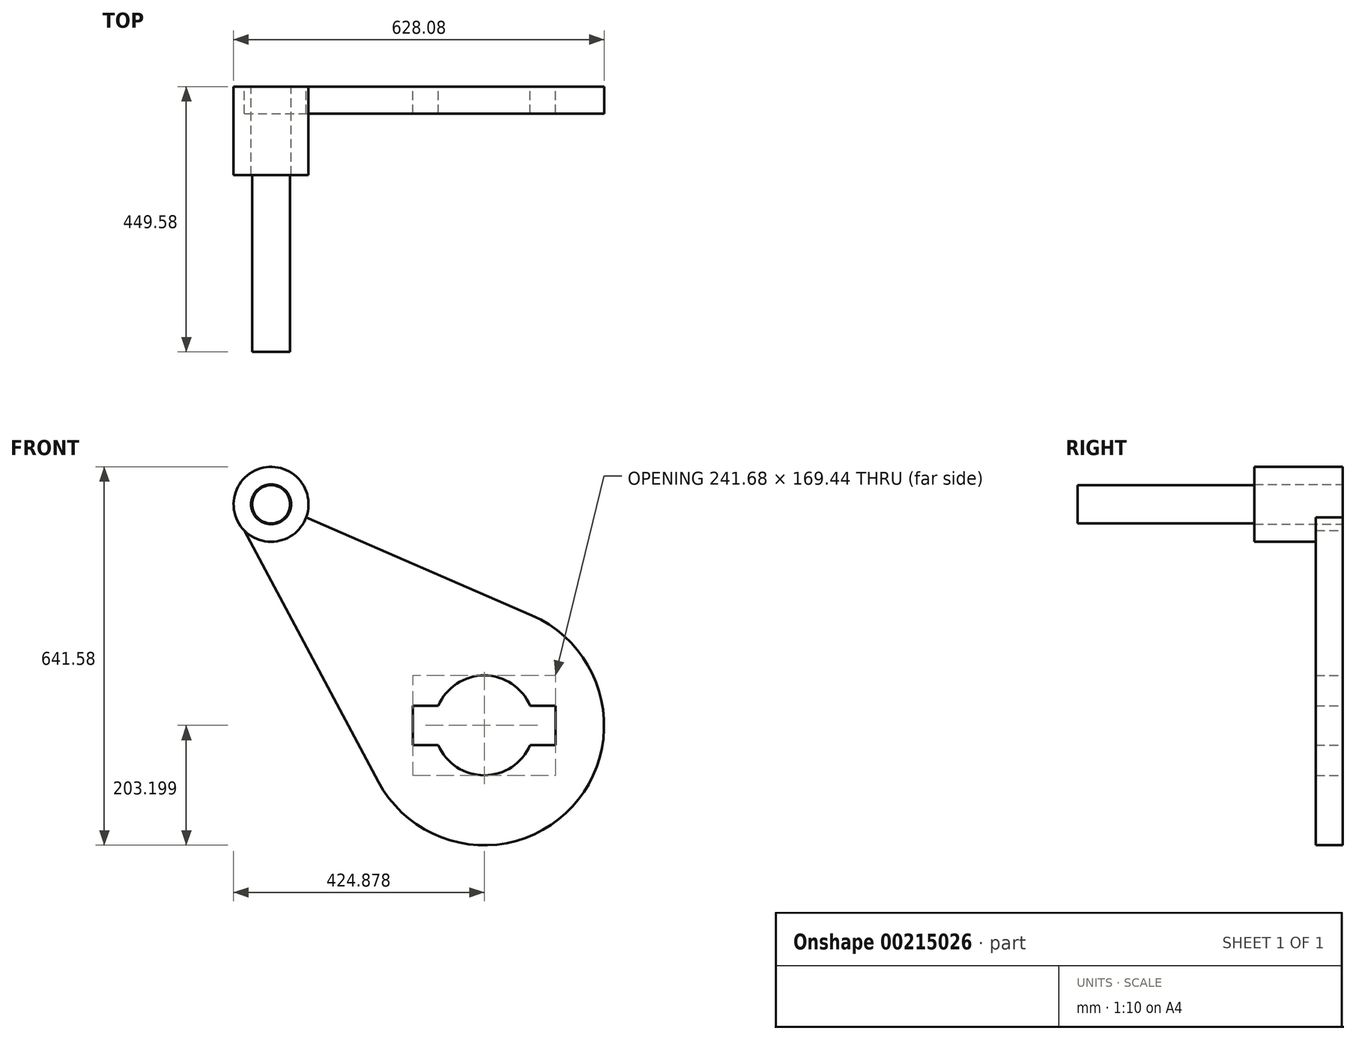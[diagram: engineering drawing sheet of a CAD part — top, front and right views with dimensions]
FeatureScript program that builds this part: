
annotation { "Feature Type Name" : "Feature", "Feature Type Description" : "" }
export const myFeature = defineFeature(function(context is Context, id is Id, definition is map)
    precondition{}
    {
        {
            var Q0;
            Q0=qCreatedBy(makeId("Front.planeOp"),FACE);
            var sketch = newSketch(context, id + "F0", { "sketchPlane" : qUnion([Q0])});
            skCircle(sketch, "E0", {"center": v(-240.54, 237.9) * mm, "radius": 63.5 * mm});
            skCircle(sketch, "E1", {"center": v(120.84, -137) * mm, "radius": 203.2 * mm});
            skLineSegment(sketch, "E2", {"start": v(-180.95, 215.96) * mm, "end": v(201.93, 49.33) * mm});
            skLineSegment(sketch, "E3", {"start": v(-285.62, 193.17) * mm, "end": v(-58.44, -232.64) * mm});
            skLineSegment(sketch, "E4.bottom", {"start": v(0, -170.09) * mm, "end": v(241.68, -170.09) * mm});
            skLineSegment(sketch, "E4.top", {"start": v(0, -103.9) * mm, "end": v(241.68, -103.9) * mm});
            skLineSegment(sketch, "E4.left", {"start": v(0, -170.09) * mm, "end": v(0, -103.9) * mm});
            skLineSegment(sketch, "E4.right", {"start": v(241.68, -170.09) * mm, "end": v(241.68, -103.9) * mm});
            skCircle(sketch, "E5", {"center": v(-240.54, 237.9) * mm, "radius": 33.9 * mm});
            skCircle(sketch, "E6", {"center": v(120.84, -137) * mm, "radius": 84.72 * mm});
            skSolve(sketch);
        }
        {
            var Q0;
            {var subQ0=sQuery(id+"F0.wireOp",EDGE,"E2");Q0=makeQuery(id+"F0.imprint","IMPRINT",FACE,{"disambiguationData":[TD([[makeQuery(id+"F0.imprint","IMPRINT",EDGE,{"derivedFrom":subQ0}),-1.0]])]});}
            var Q1;
            {var subQ4=sQuery(id+"F0.wireOp",EDGE,"E4.left");Q1=makeQuery(id+"F0.imprint","IMPRINT",FACE,{"disambiguationData":[TD([[makeQuery(id+"F0.imprint","IMPRINT",EDGE,{"derivedFrom":subQ4}),1.0]])]});}
            var Q2;
            Q2=makeQuery(id+"F0.imprint","IMPRINT",FACE,{"disambiguationData":[TD([[makeQuery(id+"F0.imprint","IMPRINT",EDGE,{"derivedFrom":sQuery(id+"F0.wireOp",EDGE,"E5")}),-1.0]])]});
            extrude(context, id + "F1", {"entities" : qUnion([Q0, Q1, Q2]), "endBound" : BoundingType.SYMMETRIC, "depth" : 45.72 * mm});
        }
        {
            var Q0;
            Q0=makeQuery(id+"F0.imprint","IMPRINT",FACE,{"disambiguationData":[TD([[makeQuery(id+"F0.imprint","IMPRINT",EDGE,{"derivedFrom":sQuery(id+"F0.wireOp",EDGE,"E5")}),-1.0]])]});
            extrude(context, id + "F2", {"entities" : qUnion([Q0]), "operationType" : NewBodyOperationType.ADD, "depth" : 127 * mm});
        }
        {
            var Q0;
            Q0=makeQuery(id+"F2.opExtrude","CAP_FACE",FACE,{"disambiguationData":[OSD([sQuery(id+"F0.wireOp",EDGE,"E0"),sQuery(id+"F0.wireOp",EDGE,"E5")])],"isStart":false});
            var sketch = newSketch(context, id + "F3", { "sketchPlane" : qUnion([Q0])});
            skCircle(sketch, "E7", {"center": v(-240.54, 237.9) * mm, "radius": 32.25 * mm});
            skSolve(sketch);
        }
        {
            var Q0;
            Q0=makeQuery(id+"F3.imprint","IMPRINT",FACE,{"disambiguationData":[TD([[makeQuery(id+"F3.imprint","IMPRINT",EDGE,{"derivedFrom":sQuery(id+"F3.wireOp",EDGE,"E7")}),1.0]])]});
            extrude(context, id + "F4", {"entities" : qUnion([Q0]), "depth" : 299.72 * mm});
        }
    });
